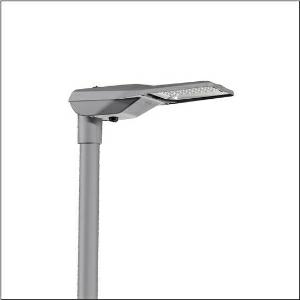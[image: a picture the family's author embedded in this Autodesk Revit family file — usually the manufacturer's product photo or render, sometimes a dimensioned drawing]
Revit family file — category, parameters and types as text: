
# Revit family: streetlight_sl_21_mini___st0_8a_5xe2c33t08gb_9409
name_source: partatom
category: Lighting Fixtures
units: mm (PartAtom-declared; Revit-internal decimal feet)

## family parameters
Cut with Voids When Loaded = No
Host = Face
Light Source = No
Part Type = Normal
Room Calculation Point = No
Round Connector Dimension = Use Diameter
Shared = No

## types (1)
- --- (1 x LED, 5940 lm, 40.4 W, 3000K)
    Apparent Load = 40 VA
    CIE Flux Codes = 38 75 97 100 100
    Color Rendering = 70
    Color Temperature = 3000K
    Default Elevation = 1800 mm
    Description = Streetlight SL 21 mini, mast luminaire, primary light control with lens, of PMMA, primary optical cover: cover, of toughened safety glass, transparent, light distribution: ST0.8a, light emission: direct distribution, primary light characteristic: asymmetric, installation type: side-entry, post-top, LED, High Power LED, rated luminous flux: 5.940lm, luminous efficacy: 147lm/W, light colour: 730, colour temperature: 3000K, control gear: D4i, control: overheat protection, constant luminous flux control, time-dependent luminous flux control, flexible luminous flux parameterisation, pre-setting: logarithmic dimming characteristic, mains connection: 220..240V, AC, 50/60Hz, start of lifetime: 40W, end of service life: 41W, reduction: 19W, luminaire housing, of diecast aluminium, powder-coated, Siteco® metallic grey (DB 702S), corrosivity category C5 mid according to DIN EN ISO 12944, please order mast flange separately, inclination adjustable: 0°, 5°, 10°, 15°, sealing non-destructively replaceable, multi-level sealing system, length: 628mm, width: 235mm, height: 110mm, mast flange for spigot size: 42mm (side-entry): 5XC10008XM4, 60/48mm (side-entry/post-top): 5XC10108XM2, 76/60mm (side-entry/post-top): 5XC10108XM1, mounting height: 4..8m, Smart Interface below and above, protection rating (complete): IP66, insulation class (complete): insulation class II (safety insulation), certification: CE, ENEC, ENEC+, VDE, impact resistance: IK10, permissible operating ambient temperature for outdoor applications: -40..+50°C, standard-compliant lighting for roads and squares, packaging unit: 1 piece

Light Distribution: ST0.8a
    Height = 110 mm
    Lamp = 1 x LED
    Lamp Light Flux = 5940 lm
    Lamp Power = 40.4 W
    Lamp count = 1
    Length = 625 mm
    Luminous efficacy = 147 lm/W
    Manufacturer = Siteco
    ModVariant = No
    Model = 5XE2C33T08GB
    Number of Poles = 1
    OnlyDefault = Yes
    Power Factor = 1
    Product Name = Streetlight SL 21 mini | ST0.8a
    Product group = mast luminaire | pylon top
    ProductGroupID = 6100
    Protection Class = Protection class II
    Protection Degree = IP 66
    RLX_Detail_Level = 1
    RLX_Emergency_Light_Flux = 0 lm
    RLX_Emergency_Type = 0
    RLX_Emergency_Type_DB = No
    RlxData = <blob elided: 26393 chars, md5=4cc661c3>
    Socket = socket
    Standby Power = 0 W
    System Light Flux = 5940 lm
    System Power = 40 W
    Type Comments = factory setting: luminous flux: 100 % | dim-lin: 254 | 812 mA
    Type Image = l_1003514.jpg
    URL = http://relux.com
    VarID = @adj_206717
    Voltage = 0 V
    Weight = 0.00 kg
    Width = 234 mm

## geometry (parser evidence)
native form markers: Blend x4, Sweep x11
no freeform markers — native parametric forms only
